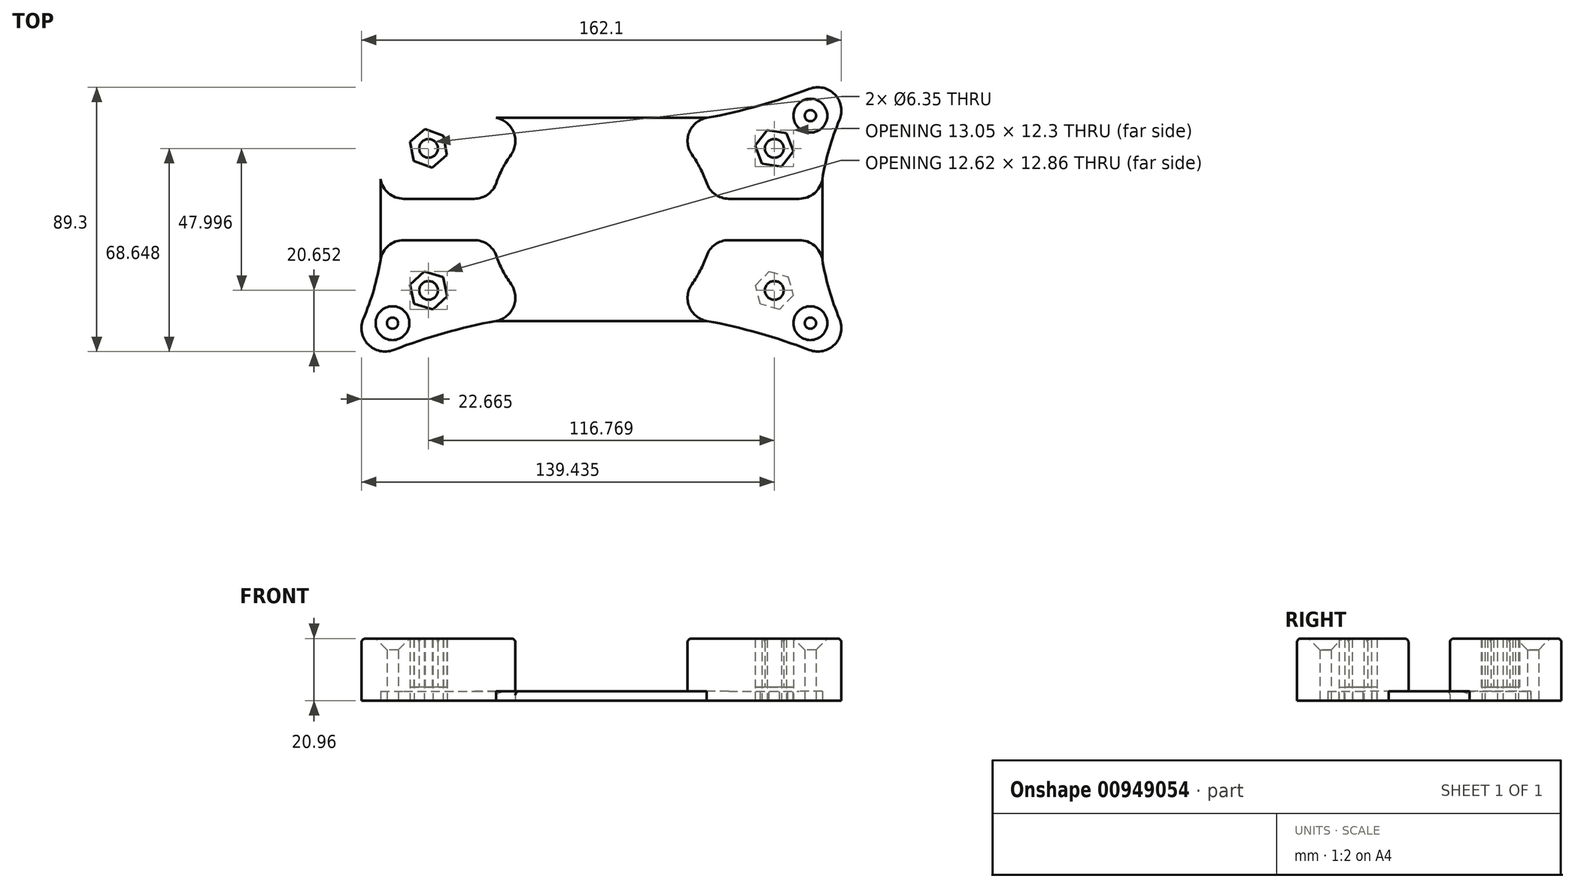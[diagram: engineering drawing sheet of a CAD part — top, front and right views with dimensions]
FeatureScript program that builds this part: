
annotation { "Feature Type Name" : "Feature", "Feature Type Description" : "" }
export const myFeature = defineFeature(function(context is Context, id is Id, definition is map)
    precondition{}
    {
        {
            var Q0;
            Q0=qCreatedBy(makeId("Top.planeOp"),FACE);
            var sketch = newSketch(context, id + "F0", { "sketchPlane" : qUnion([Q0])});
            skLineSegment(sketch, "E0.bottom", {"start": v(-102.5, 65) * mm, "end": v(102.5, 65) * mm, "construction": true});
            skLineSegment(sketch, "E0.top", {"start": v(-102.5, -65) * mm, "end": v(102.5, -65) * mm, "construction": true});
            skLineSegment(sketch, "E0.left", {"start": v(-102.5, 65) * mm, "end": v(-102.5, -65) * mm, "construction": true});
            skLineSegment(sketch, "E0.right", {"start": v(102.5, 65) * mm, "end": v(102.5, -65) * mm, "construction": true});
            skPoint(sketch, "E0.middle", {"position": v(0, 0) * mm});
            skArc(sketch, "E1", {"start": v(-79.48, 63.38) * mm, "mid": v(-98.58, 59.5) * mm, "end": v(-99.76, 40.04) * mm, "construction": true});
            skArc(sketch, "E2.MirrorC", {"start": v(79.48, 63.38) * mm, "mid": v(98.58, 59.5) * mm, "end": v(99.76, 40.04) * mm, "construction": true});
            skArc(sketch, "E3.MirrorC", {"start": v(79.48, -63.38) * mm, "mid": v(98.58, -59.5) * mm, "end": v(99.76, -40.04) * mm, "construction": true});
            skArc(sketch, "E4.MirrorC", {"start": v(-79.48, -63.38) * mm, "mid": v(-98.58, -59.5) * mm, "end": v(-99.76, -40.04) * mm, "construction": true});
            skLineSegment(sketch, "E5", {"start": v(0, 0) * mm, "end": v(0, 0) * mm});
            skPoint(sketch, "E5.endSnap0", {"position": v(0, 65) * mm});
            skLineSegment(sketch, "E6", {"start": v(0, 0) * mm, "end": v(0, -420.15) * mm, "construction": true});
            skPoint(sketch, "E7.endSnap0", {"position": v(102.5, 0) * mm});
            skLineSegment(sketch, "E8", {"start": v(0, 0) * mm, "end": v(-430.2, 0) * mm, "construction": true});
            skPoint(sketch, "E9", {"position": v(0, 45) * mm});
            skPoint(sketch, "E10", {"position": v(0, -45) * mm});
            skArc(sketch, "E11", {"start": v(-79.48, 63.38) * mm, "mid": v(0, 45) * mm, "end": v(79.48, 63.38) * mm, "construction": true});
            skArc(sketch, "E12.MirrorC", {"start": v(-79.48, -63.38) * mm, "mid": v(0, -45) * mm, "end": v(79.48, -63.38) * mm, "construction": true});
            skArc(sketch, "E13", {"start": v(99.76, 40.04) * mm, "mid": v(87.5, 0) * mm, "end": v(99.76, -40.04) * mm, "construction": true});
            skArc(sketch, "E14.MirrorC", {"start": v(-99.76, 40.04) * mm, "mid": v(-87.5, 0) * mm, "end": v(-99.76, -40.04) * mm, "construction": true});
            skCircle(sketch, "E15", {"center": v(0, 65) * mm, "radius": 3.18 * mm});
            skCircle(sketch, "E16", {"center": v(102.5, 0) * mm, "radius": 3.18 * mm});
            skCircle(sketch, "E17", {"center": v(0, -65) * mm, "radius": 3.18 * mm});
            skCircle(sketch, "E18", {"center": v(-102.5, 0) * mm, "radius": 3.17 * mm});
            skCircle(sketch, "E19", {"center": v(0, 0) * mm, "radius": 23.6 * mm, "construction": true});
            skArc(sketch, "E20.0", {"start": v(-35.5, -12.32) * mm, "mid": v(-33.37, -17.28) * mm, "end": v(-30.55, -21.87) * mm});
            skArc(sketch, "E21.1", {"start": v(-80.4, 33.6) * mm, "mid": v(-76.9, 23.8) * mm, "end": v(-74.63, 13.65) * mm});
            skArc(sketch, "E21.2", {"start": v(-70.25, 44.12) * mm, "mid": v(-53.13, 38.4) * mm, "end": v(-35.56, 34.3) * mm});
            skArc(sketch, "E21.5", {"start": v(80.4, 33.6) * mm, "mid": v(76.9, 23.8) * mm, "end": v(74.63, 13.65) * mm});
            skArc(sketch, "E21.7", {"start": v(-70.25, -44.12) * mm, "mid": v(-53.13, -38.4) * mm, "end": v(-35.56, -34.3) * mm});
            skPoint(sketch, "E22", {"position": v(-87.5, 0) * mm});
            skLineSegment(sketch, "E23.top", {"start": v(-66.8, -6.99) * mm, "end": v(-43, -6.99) * mm});
            skLineSegment(sketch, "E24.bottom", {"start": v(43, 6.98) * mm, "end": v(66.8, 6.98) * mm});
            skLineSegment(sketch, "E24.top", {"start": v(43, -6.99) * mm, "end": v(66.8, -6.99) * mm});
            skLineSegment(sketch, "E25.trimOffspring", {"start": v(-66.8, 6.99) * mm, "end": v(-43, 6.99) * mm});
            skArc(sketch, "E26.trimOffspring", {"start": v(-74.63, -13.65) * mm, "mid": v(-76.9, -23.8) * mm, "end": v(-80.4, -33.6) * mm});
            skArc(sketch, "E27.trimOffspring", {"start": v(35.5, 12.32) * mm, "mid": v(33.37, 17.28) * mm, "end": v(30.55, 21.87) * mm});
            skArc(sketch, "E28.trimOffspring", {"start": v(35.56, 34.3) * mm, "mid": v(53.13, 38.4) * mm, "end": v(70.25, 44.12) * mm});
            skArc(sketch, "E29.trimOffspring", {"start": v(74.63, -13.65) * mm, "mid": v(76.9, -23.8) * mm, "end": v(80.4, -33.6) * mm});
            skArc(sketch, "E30.trimOffspring", {"start": v(-30.55, 21.87) * mm, "mid": v(-33.37, 17.28) * mm, "end": v(-35.5, 12.32) * mm});
            skArc(sketch, "E31.trimOffspring", {"start": v(30.55, -21.87) * mm, "mid": v(33.37, -17.28) * mm, "end": v(35.5, -12.32) * mm});
            skArc(sketch, "E32.trimOffspring", {"start": v(35.56, -34.3) * mm, "mid": v(53.13, -38.4) * mm, "end": v(70.25, -44.12) * mm});
            skPoint(sketch, "E33.visualSharp", {"position": v(-73.82, 6.99) * mm});
            skArc(sketch, "E33.filletArc", {"start": v(-74.63, 13.65) * mm, "mid": v(-71.94, 8.88) * mm, "end": v(-66.8, 6.99) * mm});
            skPoint(sketch, "E34.visualSharp", {"position": v(-36.92, 6.98) * mm});
            skArc(sketch, "E34.filletArc", {"start": v(-43, 6.99) * mm, "mid": v(-38.4, 8.45) * mm, "end": v(-35.5, 12.32) * mm});
            skPoint(sketch, "E35.visualSharp", {"position": v(-19.66, 32.02) * mm});
            skArc(sketch, "E35.filletArc", {"start": v(-30.55, 21.87) * mm, "mid": v(-29.65, 29.46) * mm, "end": v(-35.56, 34.3) * mm});
            skArc(sketch, "E36.filletArc", {"start": v(-70.25, 44.12) * mm, "mid": v(-78.82, 42.23) * mm, "end": v(-80.4, 33.6) * mm});
            skPoint(sketch, "E37.visualSharp", {"position": v(-73.82, -6.99) * mm});
            skArc(sketch, "E37.filletArc", {"start": v(-66.8, -6.99) * mm, "mid": v(-71.94, -8.88) * mm, "end": v(-74.63, -13.65) * mm});
            skArc(sketch, "E38.filletArc", {"start": v(-80.4, -33.6) * mm, "mid": v(-78.82, -42.23) * mm, "end": v(-70.25, -44.12) * mm});
            skPoint(sketch, "E39.visualSharp", {"position": v(-19.66, -32.02) * mm});
            skArc(sketch, "E39.filletArc", {"start": v(-35.56, -34.3) * mm, "mid": v(-29.65, -29.46) * mm, "end": v(-30.55, -21.87) * mm});
            skPoint(sketch, "E40.visualSharp", {"position": v(-36.92, -6.99) * mm});
            skArc(sketch, "E40.filletArc", {"start": v(-35.5, -12.32) * mm, "mid": v(-38.4, -8.45) * mm, "end": v(-43, -6.99) * mm});
            skPoint(sketch, "E41.visualSharp", {"position": v(19.66, 32.02) * mm});
            skArc(sketch, "E41.filletArc", {"start": v(35.56, 34.3) * mm, "mid": v(29.65, 29.46) * mm, "end": v(30.55, 21.87) * mm});
            skArc(sketch, "E42.filletArc", {"start": v(80.4, 33.6) * mm, "mid": v(78.82, 42.23) * mm, "end": v(70.25, 44.12) * mm});
            skPoint(sketch, "E43.visualSharp", {"position": v(73.82, 6.98) * mm});
            skArc(sketch, "E43.filletArc", {"start": v(66.8, 6.98) * mm, "mid": v(71.94, 8.88) * mm, "end": v(74.63, 13.65) * mm});
            skPoint(sketch, "E44.visualSharp", {"position": v(36.92, 6.98) * mm});
            skArc(sketch, "E44.filletArc", {"start": v(35.5, 12.32) * mm, "mid": v(38.4, 8.45) * mm, "end": v(43, 6.98) * mm});
            skPoint(sketch, "E45.visualSharp", {"position": v(36.92, -6.99) * mm});
            skArc(sketch, "E45.filletArc", {"start": v(43, -6.99) * mm, "mid": v(38.4, -8.45) * mm, "end": v(35.5, -12.32) * mm});
            skPoint(sketch, "E46.visualSharp", {"position": v(73.82, -6.99) * mm});
            skArc(sketch, "E46.filletArc", {"start": v(74.63, -13.65) * mm, "mid": v(71.94, -8.88) * mm, "end": v(66.8, -6.99) * mm});
            skPoint(sketch, "E47.visualSharp", {"position": v(19.66, -32.02) * mm});
            skArc(sketch, "E47.filletArc", {"start": v(30.55, -21.87) * mm, "mid": v(29.65, -29.46) * mm, "end": v(35.56, -34.3) * mm});
            skArc(sketch, "E48.filletArc", {"start": v(70.25, -44.12) * mm, "mid": v(78.82, -42.23) * mm, "end": v(80.4, -33.6) * mm});
            skCircle(sketch, "E49", {"center": v(-58.38, 24) * mm, "radius": 3.18 * mm});
            skCircle(sketch, "E50.MirrorC", {"center": v(58.38, 24) * mm, "radius": 3.18 * mm});
            skCircle(sketch, "E51.MirrorC", {"center": v(58.38, -24) * mm, "radius": 3.18 * mm});
            skCircle(sketch, "E52.MirrorC", {"center": v(-58.38, -24) * mm, "radius": 3.18 * mm});
            skLineSegment(sketch, "E53", {"start": v(-35.56, 34.3) * mm, "end": v(35.56, 34.3) * mm});
            skLineSegment(sketch, "E54", {"start": v(-35.56, -34.3) * mm, "end": v(35.56, -34.3) * mm});
            skLineSegment(sketch, "E55", {"start": v(-74.63, 13.65) * mm, "end": v(-74.63, -13.65) * mm});
            skLineSegment(sketch, "E56", {"start": v(74.63, 13.65) * mm, "end": v(74.63, -13.65) * mm});
            skCircle(sketch, "E57.cCircle", {"center": v(-58.38, 24) * mm, "radius": 5.72 * mm, "construction": true});
            skLineSegment(sketch, "E57.0", {"start": v(-64.61, 26.18) * mm, "end": v(-59.6, 30.48) * mm});
            skLineSegment(sketch, "E57.1", {"start": v(-59.6, 30.48) * mm, "end": v(-53.38, 28.3) * mm});
            skLineSegment(sketch, "E57.2", {"start": v(-53.38, 28.3) * mm, "end": v(-52.16, 21.81) * mm});
            skLineSegment(sketch, "E57.3", {"start": v(-52.16, 21.81) * mm, "end": v(-57.17, 17.51) * mm});
            skLineSegment(sketch, "E57.4", {"start": v(-57.17, 17.51) * mm, "end": v(-63.4, 19.7) * mm});
            skLineSegment(sketch, "E57.5", {"start": v(-63.4, 19.7) * mm, "end": v(-64.61, 26.18) * mm});
            skPoint(sketch, "E57.0.midPoint", {"position": v(-62.1, 28.33) * mm});
            skCircle(sketch, "E58", {"center": v(-70.57, 35.06) * mm, "radius": 1.9 * mm});
            skCircle(sketch, "E59.MirrorC", {"center": v(-70.57, -35.06) * mm, "radius": 1.9 * mm});
            skCircle(sketch, "E60.MirrorC", {"center": v(70.57, -35.06) * mm, "radius": 1.9 * mm});
            skCircle(sketch, "E61.MirrorC", {"center": v(70.57, 35.06) * mm, "radius": 1.9 * mm});
            skCircle(sketch, "E62.cCircle", {"center": v(-58.38, -24) * mm, "radius": 5.72 * mm, "construction": true});
            skLineSegment(sketch, "E62.0", {"start": v(-64.7, -22.06) * mm, "end": v(-59.86, -17.57) * mm});
            skLineSegment(sketch, "E62.1", {"start": v(-59.86, -17.57) * mm, "end": v(-53.55, -19.5) * mm});
            skLineSegment(sketch, "E62.2", {"start": v(-53.55, -19.5) * mm, "end": v(-52.08, -25.93) * mm});
            skLineSegment(sketch, "E62.3", {"start": v(-52.08, -25.93) * mm, "end": v(-56.9, -30.43) * mm});
            skLineSegment(sketch, "E62.4", {"start": v(-56.9, -30.43) * mm, "end": v(-63.22, -28.5) * mm});
            skLineSegment(sketch, "E62.5", {"start": v(-63.22, -28.5) * mm, "end": v(-64.7, -22.06) * mm});
            skPoint(sketch, "E62.0.midPoint", {"position": v(-62.28, -19.81) * mm});
            skCircle(sketch, "E63.cCircle", {"center": v(58.38, -24) * mm, "radius": 5.72 * mm, "construction": true});
            skLineSegment(sketch, "E63.0", {"start": v(52, -22.32) * mm, "end": v(56.64, -17.63) * mm});
            skLineSegment(sketch, "E63.1", {"start": v(56.64, -17.63) * mm, "end": v(63.03, -19.3) * mm});
            skLineSegment(sketch, "E63.2", {"start": v(63.03, -19.3) * mm, "end": v(64.77, -25.67) * mm});
            skLineSegment(sketch, "E63.3", {"start": v(64.77, -25.67) * mm, "end": v(60.13, -30.36) * mm});
            skLineSegment(sketch, "E63.4", {"start": v(60.13, -30.36) * mm, "end": v(53.74, -28.69) * mm});
            skLineSegment(sketch, "E63.5", {"start": v(53.74, -28.69) * mm, "end": v(52, -22.32) * mm});
            skPoint(sketch, "E63.0.midPoint", {"position": v(54.32, -19.98) * mm});
            skCircle(sketch, "E64.cCircle", {"center": v(58.38, 24) * mm, "radius": 5.72 * mm, "construction": true});
            skLineSegment(sketch, "E64.0", {"start": v(51.86, 25) * mm, "end": v(55.99, 30.15) * mm});
            skLineSegment(sketch, "E64.1", {"start": v(55.99, 30.15) * mm, "end": v(62.51, 29.15) * mm});
            skLineSegment(sketch, "E64.2", {"start": v(62.51, 29.15) * mm, "end": v(64.9, 23) * mm});
            skLineSegment(sketch, "E64.3", {"start": v(64.9, 23) * mm, "end": v(60.78, 17.85) * mm});
            skLineSegment(sketch, "E64.4", {"start": v(60.78, 17.85) * mm, "end": v(54.26, 18.85) * mm});
            skLineSegment(sketch, "E64.5", {"start": v(54.26, 18.85) * mm, "end": v(51.86, 25) * mm});
            skPoint(sketch, "E64.0.midPoint", {"position": v(53.93, 27.57) * mm});
            skSolve(sketch);
        }
        {
            var Q0;
            Q0=makeQuery(id+"F0.imprint","IMPRINT",FACE,{"disambiguationData":[TD([[makeQuery(id+"F0.imprint","IMPRINT",EDGE,{"derivedFrom":sQuery(id+"F0.wireOp",EDGE,"E20.0")}),1.0]])]});
            extrude(context, id + "F1", {"entities" : qUnion([Q0]), "depth" : 3.17 * mm, "offsetDistance" : 25.4 * mm});
        }
        {
            var Q0;
            Q0=makeQuery(id+"F0.imprint","IMPRINT",FACE,{"disambiguationData":[TD([[makeQuery(id+"F0.imprint","IMPRINT",EDGE,{"derivedFrom":sQuery(id+"F0.wireOp",EDGE,"E21.1")}),1.0]])]});
            var Q1;
            Q1=makeQuery(id+"F0.imprint","IMPRINT",FACE,{"disambiguationData":[TD([[makeQuery(id+"F0.imprint","IMPRINT",EDGE,{"derivedFrom":sQuery(id+"F0.wireOp",EDGE,"E49")}),-1.0]])]});
            var Q2;
            Q2=makeQuery(id+"F0.imprint","IMPRINT",FACE,{"disambiguationData":[TD([[makeQuery(id+"F0.imprint","IMPRINT",EDGE,{"derivedFrom":sQuery(id+"F0.wireOp",EDGE,"E20.0")}),-1.0]])]});
            var Q3;
            Q3=makeQuery(id+"F0.imprint","IMPRINT",FACE,{"disambiguationData":[TD([[makeQuery(id+"F0.imprint","IMPRINT",EDGE,{"derivedFrom":sQuery(id+"F0.wireOp",EDGE,"E52.MirrorC")}),1.0]])]});
            var Q4;
            Q4=makeQuery(id+"F0.imprint","IMPRINT",FACE,{"disambiguationData":[TD([[makeQuery(id+"F0.imprint","IMPRINT",EDGE,{"derivedFrom":sQuery(id+"F0.wireOp",EDGE,"E21.5")}),-1.0]])]});
            var Q5;
            Q5=makeQuery(id+"F0.imprint","IMPRINT",FACE,{"disambiguationData":[TD([[makeQuery(id+"F0.imprint","IMPRINT",EDGE,{"derivedFrom":sQuery(id+"F0.wireOp",EDGE,"E50.MirrorC")}),1.0]])]});
            var Q6;
            Q6=makeQuery(id+"F0.imprint","IMPRINT",FACE,{"disambiguationData":[TD([[makeQuery(id+"F0.imprint","IMPRINT",EDGE,{"derivedFrom":sQuery(id+"F0.wireOp",EDGE,"E24.top")}),-1.0]])]});
            var Q7;
            Q7=makeQuery(id+"F0.imprint","IMPRINT",FACE,{"disambiguationData":[TD([[makeQuery(id+"F0.imprint","IMPRINT",EDGE,{"derivedFrom":sQuery(id+"F0.wireOp",EDGE,"E51.MirrorC")}),-1.0]])]});
            extrude(context, id + "F2", {"entities" : qUnion([Q0, Q1, Q2, Q3, Q4, Q5, Q6, Q7]), "operationType" : NewBodyOperationType.ADD, "depth" : 20.95 * mm, "offsetDistance" : 25.4 * mm});
        }
        {
            var Q0;
            Q0=makeQuery(id+"F2.opExtrude","CAP_EDGE",EDGE,{"disambiguationData":[OSD([sQuery(id+"F0.wireOp",EDGE,"E59.MirrorC")])],"isStart":false});
            var Q1;
            Q1=makeQuery(id+"F2.opExtrude","CAP_EDGE",EDGE,{"disambiguationData":[OSD([sQuery(id+"F0.wireOp",EDGE,"E58")])],"isStart":false});
            var Q2;
            Q2=makeQuery(id+"F2.opExtrude","CAP_EDGE",EDGE,{"disambiguationData":[OSD([sQuery(id+"F0.wireOp",EDGE,"E60.MirrorC")])],"isStart":false});
            var Q3;
            Q3=makeQuery(id+"F2.opExtrude","CAP_EDGE",EDGE,{"disambiguationData":[OSD([sQuery(id+"F0.wireOp",EDGE,"E61.MirrorC")])],"isStart":false});
            chamfer(context, id + "F3", {"entities" : qUnion([Q0, Q1, Q2, Q3]), "width" : 3.8 * mm, "tangentPropagation" : true});
        }
        {
            var Q0;
            Q0=makeQuery(id+"F0.imprint","IMPRINT",FACE,{"disambiguationData":[TD([[makeQuery(id+"F0.imprint","IMPRINT",EDGE,{"derivedFrom":sQuery(id+"F0.wireOp",EDGE,"E52.MirrorC")}),1.0]])]});
            var Q1;
            Q1=makeQuery(id+"F0.imprint","IMPRINT",FACE,{"disambiguationData":[TD([[makeQuery(id+"F0.imprint","IMPRINT",EDGE,{"derivedFrom":sQuery(id+"F0.wireOp",EDGE,"E49")}),-1.0]])]});
            var Q2;
            Q2=makeQuery(id+"F0.imprint","IMPRINT",FACE,{"disambiguationData":[TD([[makeQuery(id+"F0.imprint","IMPRINT",EDGE,{"derivedFrom":sQuery(id+"F0.wireOp",EDGE,"E50.MirrorC")}),1.0]])]});
            var Q3;
            Q3=makeQuery(id+"F0.imprint","IMPRINT",FACE,{"disambiguationData":[TD([[makeQuery(id+"F0.imprint","IMPRINT",EDGE,{"derivedFrom":sQuery(id+"F0.wireOp",EDGE,"E51.MirrorC")}),-1.0]])]});
            extrude(context, id + "F4", {"entities" : qUnion([Q0, Q1, Q2, Q3]), "operationType" : NewBodyOperationType.REMOVE, "endBound" : BoundingType.SYMMETRIC, "oppositeDirection" : true, "depth" : 9.14 * mm, "offsetDistance" : 25.4 * mm});
        }
        {
            var Q0;
            Q0=makeQuery(id+"F2.opExtrude","CAP_EDGE",EDGE,{"disambiguationData":[OSD([sQuery(id+"F0.wireOp",EDGE,"E24.top")])],"isStart":false});
            var Q1;
            Q1=makeQuery(id+"F2.opExtrude","CAP_EDGE",EDGE,{"disambiguationData":[OSD([sQuery(id+"F0.wireOp",EDGE,"E24.bottom")])],"isStart":false});
            var Q2;
            Q2=makeQuery(id+"F2.opExtrude","CAP_EDGE",EDGE,{"disambiguationData":[OSD([sQuery(id+"F0.wireOp",EDGE,"E35.filletArc")])],"isStart":false});
            var Q3;
            Q3=makeQuery(id+"F2.opExtrude","CAP_EDGE",EDGE,{"disambiguationData":[OSD([sQuery(id+"F0.wireOp",EDGE,"E40.filletArc")])],"isStart":false});
            var Q4;
            Q4=makeQuery(id+"F1.opExtrude","CAP_EDGE",EDGE,{"disambiguationData":[OSD([sQuery(id+"F0.wireOp",EDGE,"E40.filletArc")])],"isStart":false});
            var Q5;
            Q5=makeQuery(id+"F1.opExtrude","CAP_EDGE",EDGE,{"disambiguationData":[OSD([sQuery(id+"F0.wireOp",EDGE,"E35.filletArc")])],"isStart":false});
            var Q6;
            Q6=makeQuery(id+"F1.opExtrude","CAP_EDGE",EDGE,{"disambiguationData":[OSD([sQuery(id+"F0.wireOp",EDGE,"E41.filletArc")])],"isStart":false});
            var Q7;
            Q7=makeQuery(id+"F1.opExtrude","CAP_EDGE",EDGE,{"disambiguationData":[OSD([sQuery(id+"F0.wireOp",EDGE,"E46.filletArc")])],"isStart":false});
            var Q8;
            Q8=makeQuery(id+"F2.opExtrude","CAP_EDGE",EDGE,{"disambiguationData":[OSD([sQuery(id+"F0.wireOp",EDGE,"E49")])],"isStart":false});
            var Q9;
            Q9=makeQuery(id+"F2.opExtrude","CAP_EDGE",EDGE,{"disambiguationData":[OSD([sQuery(id+"F0.wireOp",EDGE,"E50.MirrorC")])],"isStart":false});
            var Q10;
            Q10=makeQuery(id+"F2.opExtrude","CAP_EDGE",EDGE,{"disambiguationData":[OSD([sQuery(id+"F0.wireOp",EDGE,"E52.MirrorC")])],"isStart":false});
            var Q11;
            Q11=makeQuery(id+"F2.opExtrude","CAP_EDGE",EDGE,{"disambiguationData":[OSD([sQuery(id+"F0.wireOp",EDGE,"E51.MirrorC")])],"isStart":false});
            fillet(context, id + "F5", {"entities" : qUnion([Q0, Q1, Q2, Q3, Q4, Q5, Q6, Q7, Q8, Q9, Q10, Q11]), "radius" : 1.27 * mm, "tangentPropagation" : true, "allowEdgeOverflow" : false});
        }
    });
